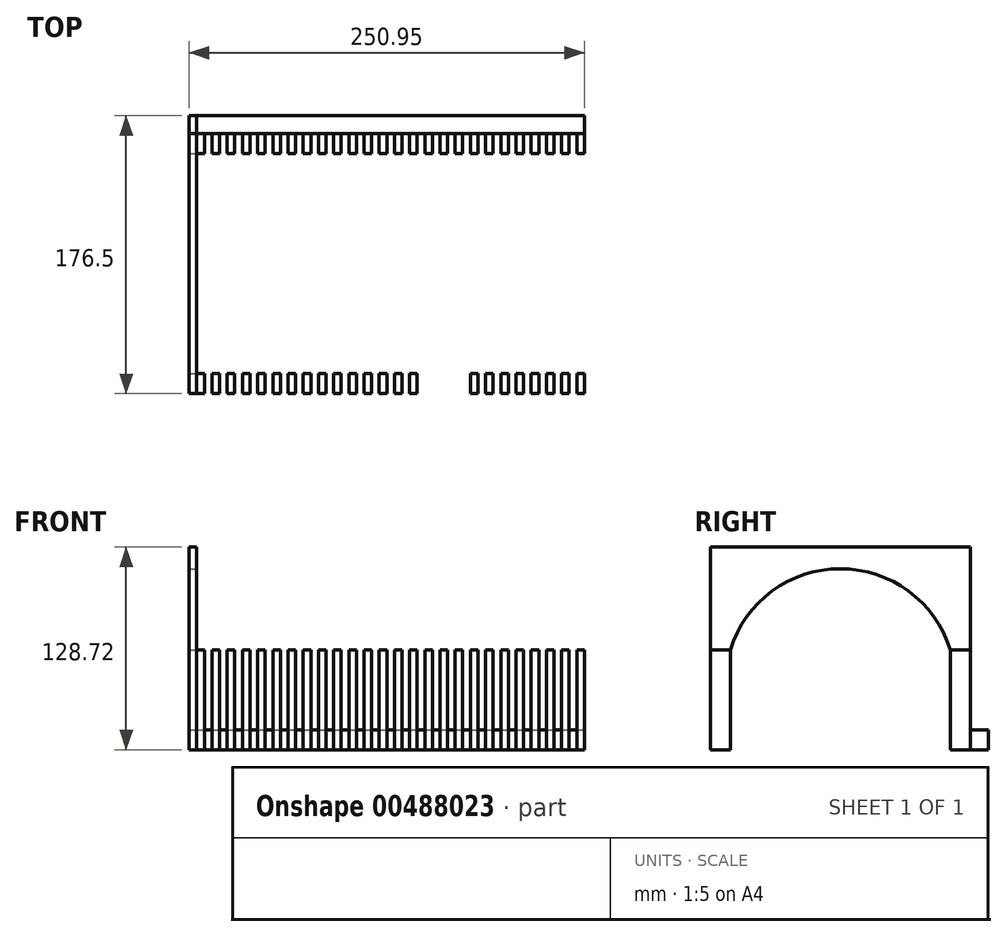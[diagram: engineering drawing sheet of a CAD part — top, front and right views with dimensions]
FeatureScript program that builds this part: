
annotation { "Feature Type Name" : "Feature", "Feature Type Description" : "" }
export const myFeature = defineFeature(function(context is Context, id is Id, definition is map)
    precondition{}
    {
        {
            var Q0;
            Q0=qCreatedBy(makeId("Top.planeOp"),FACE);
            var sketch = newSketch(context, id + "F0", { "sketchPlane" : qUnion([Q0])});
            skLineSegment(sketch, "E0.bottom", {"start": v(-94.37, 0) * mm, "end": v(-89.54, 0) * mm});
            skLineSegment(sketch, "E0.top", {"start": v(-94.37, 12.7) * mm, "end": v(-89.54, 12.7) * mm});
            skLineSegment(sketch, "E0.left", {"start": v(-94.37, 0) * mm, "end": v(-94.37, 12.7) * mm});
            skLineSegment(sketch, "E0.right", {"start": v(-89.54, 0) * mm, "end": v(-89.54, 12.7) * mm});
            skLineSegment(sketch, "E1.1.0.0", {"start": v(-84.71, 0) * mm, "end": v(-84.71, 12.7) * mm});
            skLineSegment(sketch, "E1.2.0.0", {"start": v(-79.89, 0) * mm, "end": v(-79.89, 12.7) * mm});
            skLineSegment(sketch, "E1.3.0.0", {"start": v(-75.06, 0) * mm, "end": v(-75.06, 12.7) * mm});
            skLineSegment(sketch, "E1.4.0.0", {"start": v(-70.24, 0) * mm, "end": v(-70.24, 12.7) * mm});
            skLineSegment(sketch, "E1.5.0.0", {"start": v(-65.4, 0) * mm, "end": v(-65.4, 12.7) * mm});
            skLineSegment(sketch, "E1.6.0.0", {"start": v(-60.58, 0) * mm, "end": v(-60.58, 12.7) * mm});
            skLineSegment(sketch, "E1.7.0.0", {"start": v(-55.76, 0) * mm, "end": v(-55.76, 12.7) * mm});
            skLineSegment(sketch, "E1.8.0.0", {"start": v(-50.93, 0) * mm, "end": v(-50.93, 12.7) * mm});
            skLineSegment(sketch, "E1.9.0.0", {"start": v(-46.1, 0) * mm, "end": v(-46.1, 12.7) * mm});
            skLineSegment(sketch, "E1.10.0.0", {"start": v(-41.28, 0) * mm, "end": v(-41.28, 12.7) * mm});
            skLineSegment(sketch, "E1.11.0.0", {"start": v(-36.45, 0) * mm, "end": v(-36.45, 12.7) * mm});
            skLineSegment(sketch, "E1.12.0.0", {"start": v(-31.63, 0) * mm, "end": v(-31.63, 12.7) * mm});
            skLineSegment(sketch, "E1.13.0.0", {"start": v(-26.8, 0) * mm, "end": v(-26.8, 12.7) * mm});
            skLineSegment(sketch, "E1.14.0.0", {"start": v(-21.98, 0) * mm, "end": v(-21.98, 12.7) * mm});
            skLineSegment(sketch, "E1.15.0.0", {"start": v(-17.15, 0) * mm, "end": v(-17.15, 12.7) * mm});
            skLineSegment(sketch, "E1.16.0.0", {"start": v(-12.32, 0) * mm, "end": v(-12.32, 12.7) * mm});
            skLineSegment(sketch, "E1.17.0.0", {"start": v(-7.5, 0) * mm, "end": v(-7.5, 12.7) * mm});
            skLineSegment(sketch, "E1.18.0.0", {"start": v(-2.67, 0) * mm, "end": v(-2.67, 12.7) * mm});
            skLineSegment(sketch, "E1.19.0.0", {"start": v(2.15, 0) * mm, "end": v(2.15, 12.7) * mm});
            skLineSegment(sketch, "E1.20.0.0", {"start": v(6.98, 0) * mm, "end": v(6.98, 12.7) * mm});
            skLineSegment(sketch, "E1.21.0.0", {"start": v(11.8, 0) * mm, "end": v(11.8, 12.7) * mm});
            skLineSegment(sketch, "E1.22.0.0", {"start": v(16.63, 0) * mm, "end": v(16.63, 12.7) * mm});
            skLineSegment(sketch, "E1.23.0.0", {"start": v(21.46, 0) * mm, "end": v(21.46, 12.7) * mm});
            skLineSegment(sketch, "E1.24.0.0", {"start": v(26.28, 0) * mm, "end": v(26.28, 12.7) * mm});
            skLineSegment(sketch, "E1.25.0.0", {"start": v(31.11, 0) * mm, "end": v(31.11, 12.7) * mm});
            skLineSegment(sketch, "E1.26.0.0", {"start": v(35.94, 0) * mm, "end": v(35.94, 12.7) * mm});
            skLineSegment(sketch, "E1.27.0.0", {"start": v(40.76, 0) * mm, "end": v(40.76, 12.7) * mm});
            skLineSegment(sketch, "E1.28.0.0", {"start": v(45.59, 0) * mm, "end": v(45.59, 12.7) * mm});
            skLineSegment(sketch, "E1.29.0.0", {"start": v(50.41, 0) * mm, "end": v(50.41, 12.7) * mm});
            skLineSegment(sketch, "E1.30.0.0", {"start": v(55.24, 0) * mm, "end": v(55.24, 12.7) * mm});
            skLineSegment(sketch, "E1.31.0.0", {"start": v(60.07, 0) * mm, "end": v(60.07, 12.7) * mm});
            skLineSegment(sketch, "E1.32.0.0", {"start": v(64.9, 0) * mm, "end": v(64.9, 12.7) * mm});
            skLineSegment(sketch, "E1.33.0.0", {"start": v(69.72, 0) * mm, "end": v(69.72, 12.7) * mm});
            skLineSegment(sketch, "E1.34.0.0", {"start": v(74.54, 0) * mm, "end": v(74.54, 12.7) * mm});
            skLineSegment(sketch, "E1.35.0.0", {"start": v(79.37, 0) * mm, "end": v(79.37, 12.7) * mm});
            skLineSegment(sketch, "E1.36.0.0", {"start": v(84.2, 0) * mm, "end": v(84.2, 12.7) * mm});
            skLineSegment(sketch, "E1.37.0.0", {"start": v(89.02, 0) * mm, "end": v(89.02, 12.7) * mm});
            skLineSegment(sketch, "E1.38.0.0", {"start": v(93.85, 0) * mm, "end": v(93.85, 12.7) * mm});
            skLineSegment(sketch, "E1.39.0.0", {"start": v(98.67, 0) * mm, "end": v(98.67, 12.7) * mm});
            skLineSegment(sketch, "E1.40.0.0", {"start": v(103.5, 0) * mm, "end": v(103.5, 12.7) * mm});
            skLineSegment(sketch, "E1.41.0.0", {"start": v(108.33, 0) * mm, "end": v(108.33, 12.7) * mm});
            skLineSegment(sketch, "E1.42.0.0", {"start": v(113.15, 0) * mm, "end": v(113.15, 12.7) * mm});
            skLineSegment(sketch, "E1.43.0.0", {"start": v(117.98, 0) * mm, "end": v(117.98, 12.7) * mm});
            skLineSegment(sketch, "E1.44.0.0", {"start": v(122.8, 0) * mm, "end": v(122.8, 12.7) * mm});
            skLineSegment(sketch, "E1.45.0.0", {"start": v(127.63, 0) * mm, "end": v(127.63, 12.7) * mm});
            skLineSegment(sketch, "E1.46.0.0", {"start": v(132.46, 0) * mm, "end": v(132.46, 12.7) * mm});
            skLineSegment(sketch, "E1.47.0.0", {"start": v(137.28, 0) * mm, "end": v(137.28, 12.7) * mm});
            skLineSegment(sketch, "E1.48.0.0", {"start": v(142.1, 0) * mm, "end": v(142.1, 12.7) * mm});
            skLineSegment(sketch, "E1.49.0.0", {"start": v(146.93, 0) * mm, "end": v(146.93, 12.7) * mm});
            skLineSegment(sketch, "E1.direction1", {"start": v(-89.54, 0) * mm, "end": v(-84.71, 0) * mm, "construction": true});
            skLineSegment(sketch, "E2", {"start": v(-84.71, 12.7) * mm, "end": v(-79.89, 12.7) * mm});
            skLineSegment(sketch, "E3", {"start": v(-75.06, 12.7) * mm, "end": v(-70.24, 12.7) * mm});
            skLineSegment(sketch, "E4", {"start": v(-65.4, 12.7) * mm, "end": v(-60.58, 12.7) * mm});
            skLineSegment(sketch, "E5", {"start": v(-55.76, 12.7) * mm, "end": v(-50.93, 12.7) * mm});
            skLineSegment(sketch, "E6", {"start": v(-46.1, 12.7) * mm, "end": v(-41.28, 12.7) * mm});
            skLineSegment(sketch, "E7", {"start": v(-36.45, 12.7) * mm, "end": v(-31.63, 12.7) * mm});
            skLineSegment(sketch, "E8", {"start": v(-26.8, 12.7) * mm, "end": v(-21.98, 12.7) * mm});
            skLineSegment(sketch, "E9", {"start": v(-17.15, 12.7) * mm, "end": v(-12.32, 12.7) * mm});
            skLineSegment(sketch, "E10", {"start": v(-7.5, 12.7) * mm, "end": v(-2.67, 12.7) * mm});
            skLineSegment(sketch, "E11", {"start": v(2.15, 12.7) * mm, "end": v(6.98, 12.7) * mm});
            skLineSegment(sketch, "E12", {"start": v(21.46, 12.7) * mm, "end": v(26.28, 12.7) * mm});
            skLineSegment(sketch, "E13", {"start": v(31.11, 12.7) * mm, "end": v(35.94, 12.7) * mm});
            skLineSegment(sketch, "E14", {"start": v(40.76, 12.7) * mm, "end": v(45.59, 12.7) * mm});
            skLineSegment(sketch, "E15", {"start": v(50.41, 12.7) * mm, "end": v(55.24, 12.7) * mm});
            skLineSegment(sketch, "E16", {"start": v(60.07, 12.7) * mm, "end": v(64.9, 12.7) * mm});
            skLineSegment(sketch, "E17", {"start": v(69.72, 12.7) * mm, "end": v(74.54, 12.7) * mm});
            skLineSegment(sketch, "E18", {"start": v(79.37, 12.7) * mm, "end": v(84.2, 12.7) * mm});
            skLineSegment(sketch, "E19", {"start": v(89.02, 12.7) * mm, "end": v(93.85, 12.7) * mm});
            skLineSegment(sketch, "E20", {"start": v(98.67, 12.7) * mm, "end": v(103.5, 12.7) * mm});
            skLineSegment(sketch, "E21", {"start": v(108.33, 12.7) * mm, "end": v(113.15, 12.7) * mm});
            skLineSegment(sketch, "E22", {"start": v(117.98, 12.7) * mm, "end": v(122.8, 12.7) * mm});
            skLineSegment(sketch, "E23", {"start": v(127.63, 12.7) * mm, "end": v(132.46, 12.7) * mm});
            skLineSegment(sketch, "E24", {"start": v(137.28, 12.7) * mm, "end": v(142.1, 12.7) * mm});
            skLineSegment(sketch, "E25", {"start": v(-84.71, 0) * mm, "end": v(-79.89, 0) * mm});
            skLineSegment(sketch, "E26", {"start": v(-75.06, 0) * mm, "end": v(-70.24, 0) * mm});
            skLineSegment(sketch, "E27", {"start": v(-65.4, 0) * mm, "end": v(-60.58, 0) * mm});
            skLineSegment(sketch, "E28", {"start": v(-55.76, 0) * mm, "end": v(-50.93, 0) * mm});
            skLineSegment(sketch, "E29", {"start": v(-46.1, 0) * mm, "end": v(-41.28, 0) * mm});
            skLineSegment(sketch, "E30", {"start": v(-36.45, 0) * mm, "end": v(-31.63, 0) * mm});
            skLineSegment(sketch, "E31", {"start": v(-26.8, 0) * mm, "end": v(-21.98, 0) * mm});
            skLineSegment(sketch, "E32", {"start": v(-17.15, 0) * mm, "end": v(-12.32, 0) * mm});
            skLineSegment(sketch, "E33", {"start": v(-7.5, 0) * mm, "end": v(-2.67, 0) * mm});
            skLineSegment(sketch, "E34", {"start": v(2.15, 0) * mm, "end": v(6.98, 0) * mm});
            skLineSegment(sketch, "E35", {"start": v(21.46, 0) * mm, "end": v(26.28, 0) * mm});
            skLineSegment(sketch, "E36", {"start": v(11.8, 12.7) * mm, "end": v(16.63, 12.7) * mm});
            skLineSegment(sketch, "E37", {"start": v(16.63, 0) * mm, "end": v(11.8, 0) * mm});
            skLineSegment(sketch, "E38", {"start": v(31.11, 0) * mm, "end": v(35.94, 0) * mm});
            skLineSegment(sketch, "E39", {"start": v(40.76, 0) * mm, "end": v(45.59, 0) * mm});
            skLineSegment(sketch, "E40", {"start": v(50.41, 0) * mm, "end": v(55.24, 0) * mm});
            skLineSegment(sketch, "E41", {"start": v(60.07, 0) * mm, "end": v(64.9, 0) * mm});
            skLineSegment(sketch, "E42", {"start": v(69.72, 0) * mm, "end": v(74.54, 0) * mm});
            skLineSegment(sketch, "E43", {"start": v(79.37, 0) * mm, "end": v(84.2, 0) * mm});
            skLineSegment(sketch, "E44", {"start": v(89.02, 0) * mm, "end": v(93.85, 0) * mm});
            skLineSegment(sketch, "E45", {"start": v(98.67, 0) * mm, "end": v(103.5, 0) * mm});
            skLineSegment(sketch, "E46", {"start": v(108.33, 0) * mm, "end": v(113.15, 0) * mm});
            skLineSegment(sketch, "E47", {"start": v(117.98, 0) * mm, "end": v(122.8, 0) * mm});
            skLineSegment(sketch, "E48", {"start": v(127.63, 0) * mm, "end": v(132.46, 0) * mm});
            skLineSegment(sketch, "E49", {"start": v(137.28, 0) * mm, "end": v(142.1, 0) * mm});
            skLineSegment(sketch, "E50", {"start": v(146.93, 12.7) * mm, "end": v(151.76, 12.7) * mm});
            skLineSegment(sketch, "E51", {"start": v(151.76, 12.7) * mm, "end": v(151.76, 0) * mm});
            skLineSegment(sketch, "E52", {"start": v(151.76, 0) * mm, "end": v(146.93, 0) * mm});
            skLineSegment(sketch, "E53", {"start": v(-94.37, 0) * mm, "end": v(151.76, 0) * mm, "construction": true});
            skLineSegment(sketch, "E54.bottom", {"start": v(-94.37, 12.7) * mm, "end": v(151.76, 12.7) * mm});
            skLineSegment(sketch, "E54.top", {"start": v(-94.37, 24.1) * mm, "end": v(151.76, 24.1) * mm});
            skLineSegment(sketch, "E54.left", {"start": v(-94.37, 12.7) * mm, "end": v(-94.37, 24.1) * mm});
            skLineSegment(sketch, "E54.right", {"start": v(151.76, 12.7) * mm, "end": v(151.76, 24.1) * mm});
            skLineSegment(sketch, "E55", {"start": v(-124.36, -69.85) * mm, "end": v(197.2, -69.85) * mm, "construction": true});
            skLineSegment(sketch, "E56.MirrorCS", {"start": v(-89.54, -139.7) * mm, "end": v(-84.71, -139.7) * mm, "construction": true});
            skLineSegment(sketch, "E57.MirrorCS", {"start": v(108.33, -139.7) * mm, "end": v(113.15, -139.7) * mm});
            skLineSegment(sketch, "E58.MirrorCS", {"start": v(-55.76, -139.7) * mm, "end": v(-50.93, -139.7) * mm});
            skLineSegment(sketch, "E59.MirrorCS", {"start": v(-94.37, -139.7) * mm, "end": v(-89.54, -139.7) * mm});
            skLineSegment(sketch, "E60.MirrorCS", {"start": v(79.37, -139.7) * mm, "end": v(84.2, -139.7) * mm});
            skLineSegment(sketch, "E61.MirrorCS", {"start": v(108.33, -152.4) * mm, "end": v(113.15, -152.4) * mm});
            skLineSegment(sketch, "E62.MirrorCS", {"start": v(-26.8, -152.4) * mm, "end": v(-21.98, -152.4) * mm});
            skLineSegment(sketch, "E63.MirrorCS", {"start": v(2.15, -139.7) * mm, "end": v(6.98, -139.7) * mm});
            skLineSegment(sketch, "E64.MirrorCS", {"start": v(-7.5, -139.7) * mm, "end": v(-2.67, -139.7) * mm});
            skLineSegment(sketch, "E65.MirrorCS", {"start": v(-55.76, -152.4) * mm, "end": v(-50.93, -152.4) * mm});
            skLineSegment(sketch, "E66.MirrorCS", {"start": v(98.67, -139.7) * mm, "end": v(103.5, -139.7) * mm});
            skLineSegment(sketch, "E67.MirrorCS", {"start": v(40.76, -152.4) * mm, "end": v(45.59, -152.4) * mm});
            skLineSegment(sketch, "E68.MirrorCS", {"start": v(-94.37, -139.7) * mm, "end": v(151.76, -139.7) * mm, "construction": true});
            skLineSegment(sketch, "E69.MirrorCS", {"start": v(31.11, -152.4) * mm, "end": v(35.94, -152.4) * mm});
            skLineSegment(sketch, "E70.MirrorCS", {"start": v(-46.1, -139.7) * mm, "end": v(-41.28, -139.7) * mm});
            skLineSegment(sketch, "E71.MirrorCS", {"start": v(11.8, -152.4) * mm, "end": v(16.63, -152.4) * mm});
            skLineSegment(sketch, "E72.MirrorCS", {"start": v(21.46, -139.7) * mm, "end": v(26.28, -139.7) * mm});
            skLineSegment(sketch, "E73.MirrorCS", {"start": v(-75.06, -152.4) * mm, "end": v(-70.24, -152.4) * mm});
            skLineSegment(sketch, "E74.MirrorCS", {"start": v(146.93, -152.4) * mm, "end": v(151.76, -152.4) * mm});
            skLineSegment(sketch, "E75.MirrorCS", {"start": v(-84.71, -152.4) * mm, "end": v(-79.89, -152.4) * mm});
            skLineSegment(sketch, "E76.MirrorCS", {"start": v(2.15, -152.4) * mm, "end": v(6.98, -152.4) * mm});
            skLineSegment(sketch, "E77.MirrorCS", {"start": v(-17.15, -152.4) * mm, "end": v(-12.32, -152.4) * mm});
            skLineSegment(sketch, "E78.MirrorCS", {"start": v(40.76, -139.7) * mm, "end": v(45.59, -139.7) * mm});
            skLineSegment(sketch, "E79.MirrorCS", {"start": v(-36.45, -152.4) * mm, "end": v(-31.63, -152.4) * mm});
            skLineSegment(sketch, "E80.MirrorCS", {"start": v(127.63, -152.4) * mm, "end": v(132.46, -152.4) * mm});
            skLineSegment(sketch, "E81.MirrorCS", {"start": v(127.63, -139.7) * mm, "end": v(132.46, -139.7) * mm});
            skLineSegment(sketch, "E82.MirrorCS", {"start": v(16.63, -139.7) * mm, "end": v(11.8, -139.7) * mm});
            skLineSegment(sketch, "E83.MirrorCS", {"start": v(-94.37, -152.4) * mm, "end": v(-89.54, -152.4) * mm});
            skLineSegment(sketch, "E84.MirrorCS", {"start": v(117.98, -139.7) * mm, "end": v(122.8, -139.7) * mm});
            skLineSegment(sketch, "E85.MirrorCS", {"start": v(137.28, -152.4) * mm, "end": v(142.1, -152.4) * mm});
            skLineSegment(sketch, "E86.MirrorCS", {"start": v(79.37, -152.4) * mm, "end": v(84.2, -152.4) * mm});
            skLineSegment(sketch, "E87.MirrorCS", {"start": v(31.11, -139.7) * mm, "end": v(35.94, -139.7) * mm});
            skLineSegment(sketch, "E88.MirrorCS", {"start": v(-65.4, -152.4) * mm, "end": v(-60.58, -152.4) * mm});
            skLineSegment(sketch, "E89.MirrorCS", {"start": v(-46.1, -152.4) * mm, "end": v(-41.28, -152.4) * mm});
            skLineSegment(sketch, "E90.MirrorCS", {"start": v(-26.8, -139.7) * mm, "end": v(-21.98, -139.7) * mm});
            skLineSegment(sketch, "E91.MirrorCS", {"start": v(-94.37, -152.4) * mm, "end": v(151.76, -152.4) * mm});
            skLineSegment(sketch, "E92.MirrorCS", {"start": v(117.98, -152.4) * mm, "end": v(122.8, -152.4) * mm});
            skLineSegment(sketch, "E93.MirrorCS", {"start": v(89.02, -139.7) * mm, "end": v(93.85, -139.7) * mm});
            skLineSegment(sketch, "E94.MirrorCS", {"start": v(21.46, -152.4) * mm, "end": v(26.28, -152.4) * mm});
            skLineSegment(sketch, "E95.MirrorCS", {"start": v(69.72, -152.4) * mm, "end": v(74.54, -152.4) * mm});
            skLineSegment(sketch, "E96.MirrorCS", {"start": v(-65.4, -139.7) * mm, "end": v(-60.58, -139.7) * mm});
            skLineSegment(sketch, "E97.MirrorCS", {"start": v(-17.15, -139.7) * mm, "end": v(-12.32, -139.7) * mm});
            skLineSegment(sketch, "E98.MirrorCS", {"start": v(-84.71, -139.7) * mm, "end": v(-79.89, -139.7) * mm});
            skLineSegment(sketch, "E99.MirrorCS", {"start": v(60.07, -152.4) * mm, "end": v(64.9, -152.4) * mm});
            skLineSegment(sketch, "E100.MirrorCS", {"start": v(60.07, -139.7) * mm, "end": v(64.9, -139.7) * mm});
            skLineSegment(sketch, "E101.MirrorCS", {"start": v(137.28, -139.7) * mm, "end": v(142.1, -139.7) * mm});
            skLineSegment(sketch, "E102.MirrorCS", {"start": v(50.41, -152.4) * mm, "end": v(55.24, -152.4) * mm});
            skLineSegment(sketch, "E103.MirrorCS", {"start": v(89.02, -152.4) * mm, "end": v(93.85, -152.4) * mm});
            skLineSegment(sketch, "E104.MirrorCS", {"start": v(50.41, -139.7) * mm, "end": v(55.24, -139.7) * mm});
            skLineSegment(sketch, "E105.MirrorCS", {"start": v(-75.06, -139.7) * mm, "end": v(-70.24, -139.7) * mm});
            skLineSegment(sketch, "E106.MirrorCS", {"start": v(-7.5, -152.4) * mm, "end": v(-2.67, -152.4) * mm});
            skLineSegment(sketch, "E107.MirrorCS", {"start": v(69.72, -139.7) * mm, "end": v(74.54, -139.7) * mm});
            skLineSegment(sketch, "E108.MirrorCS", {"start": v(-36.45, -139.7) * mm, "end": v(-31.63, -139.7) * mm});
            skLineSegment(sketch, "E109.MirrorCS", {"start": v(98.67, -152.4) * mm, "end": v(103.5, -152.4) * mm});
            skLineSegment(sketch, "E110.MirrorCS", {"start": v(151.76, -139.7) * mm, "end": v(146.93, -139.7) * mm});
            skLineSegment(sketch, "E111.MirrorCS", {"start": v(151.76, -152.4) * mm, "end": v(151.76, -163.8) * mm});
            skLineSegment(sketch, "E112.MirrorCS", {"start": v(60.07, -139.7) * mm, "end": v(60.07, -152.4) * mm});
            skLineSegment(sketch, "E113.MirrorCS", {"start": v(137.28, -139.7) * mm, "end": v(137.28, -152.4) * mm});
            skLineSegment(sketch, "E114.MirrorCS", {"start": v(93.85, -139.7) * mm, "end": v(93.85, -152.4) * mm});
            skLineSegment(sketch, "E115.MirrorCS", {"start": v(55.24, -139.7) * mm, "end": v(55.24, -152.4) * mm});
            skLineSegment(sketch, "E116.MirrorCS", {"start": v(132.46, -139.7) * mm, "end": v(132.46, -152.4) * mm});
            skLineSegment(sketch, "E117.MirrorCS", {"start": v(11.8, -139.7) * mm, "end": v(11.8, -152.4) * mm});
            skLineSegment(sketch, "E118.MirrorCS", {"start": v(50.41, -139.7) * mm, "end": v(50.41, -152.4) * mm});
            skLineSegment(sketch, "E119.MirrorCS", {"start": v(6.98, -139.7) * mm, "end": v(6.98, -152.4) * mm});
            skLineSegment(sketch, "E120.MirrorCS", {"start": v(84.2, -139.7) * mm, "end": v(84.2, -152.4) * mm});
            skLineSegment(sketch, "E121.MirrorCS", {"start": v(-65.4, -139.7) * mm, "end": v(-65.4, -152.4) * mm});
            skLineSegment(sketch, "E122.MirrorCS", {"start": v(-94.37, -139.7) * mm, "end": v(-94.37, -152.4) * mm});
            skLineSegment(sketch, "E123.MirrorCS", {"start": v(-31.63, -139.7) * mm, "end": v(-31.63, -152.4) * mm});
            skLineSegment(sketch, "E124.MirrorCS", {"start": v(-36.45, -139.7) * mm, "end": v(-36.45, -152.4) * mm});
            skLineSegment(sketch, "E125.MirrorCS", {"start": v(45.59, -139.7) * mm, "end": v(45.59, -152.4) * mm});
            skLineSegment(sketch, "E126.MirrorCS", {"start": v(2.15, -139.7) * mm, "end": v(2.15, -152.4) * mm});
            skLineSegment(sketch, "E127.MirrorCS", {"start": v(146.93, -139.7) * mm, "end": v(146.93, -152.4) * mm});
            skLineSegment(sketch, "E128.MirrorCS", {"start": v(-94.37, -163.8) * mm, "end": v(151.76, -163.8) * mm});
            skLineSegment(sketch, "E129.MirrorCS", {"start": v(26.28, -139.7) * mm, "end": v(26.28, -152.4) * mm});
            skLineSegment(sketch, "E130.MirrorCS", {"start": v(103.5, -139.7) * mm, "end": v(103.5, -152.4) * mm});
            skLineSegment(sketch, "E131.MirrorCS", {"start": v(-7.5, -139.7) * mm, "end": v(-7.5, -152.4) * mm});
            skLineSegment(sketch, "E132.MirrorCS", {"start": v(-94.37, -152.4) * mm, "end": v(-94.37, -163.8) * mm});
            skLineSegment(sketch, "E133.MirrorCS", {"start": v(-60.58, -139.7) * mm, "end": v(-60.58, -152.4) * mm});
            skLineSegment(sketch, "E134.MirrorCS", {"start": v(142.1, -139.7) * mm, "end": v(142.1, -152.4) * mm});
            skLineSegment(sketch, "E135.MirrorCS", {"start": v(64.9, -139.7) * mm, "end": v(64.9, -152.4) * mm});
            skLineSegment(sketch, "E136.MirrorCS", {"start": v(-70.24, -139.7) * mm, "end": v(-70.24, -152.4) * mm});
            skLineSegment(sketch, "E137.MirrorCS", {"start": v(-84.71, -139.7) * mm, "end": v(-84.71, -152.4) * mm});
            skLineSegment(sketch, "E138.MirrorCS", {"start": v(-12.32, -139.7) * mm, "end": v(-12.32, -152.4) * mm});
            skLineSegment(sketch, "E139.MirrorCS", {"start": v(-55.76, -139.7) * mm, "end": v(-55.76, -152.4) * mm});
            skLineSegment(sketch, "E140.MirrorCS", {"start": v(122.8, -139.7) * mm, "end": v(122.8, -152.4) * mm});
            skLineSegment(sketch, "E141.MirrorCS", {"start": v(16.63, -139.7) * mm, "end": v(16.63, -152.4) * mm});
            skLineSegment(sketch, "E142.MirrorCS", {"start": v(79.37, -139.7) * mm, "end": v(79.37, -152.4) * mm});
            skLineSegment(sketch, "E143.MirrorCS", {"start": v(-21.98, -139.7) * mm, "end": v(-21.98, -152.4) * mm});
            skLineSegment(sketch, "E144.MirrorCS", {"start": v(-50.93, -139.7) * mm, "end": v(-50.93, -152.4) * mm});
            skLineSegment(sketch, "E145.MirrorCS", {"start": v(-41.28, -139.7) * mm, "end": v(-41.28, -152.4) * mm});
            skLineSegment(sketch, "E146.MirrorCS", {"start": v(21.46, -139.7) * mm, "end": v(21.46, -152.4) * mm});
            skLineSegment(sketch, "E147.MirrorCS", {"start": v(98.67, -139.7) * mm, "end": v(98.67, -152.4) * mm});
            skLineSegment(sketch, "E148.MirrorCS", {"start": v(-26.8, -139.7) * mm, "end": v(-26.8, -152.4) * mm});
            skLineSegment(sketch, "E149.MirrorCS", {"start": v(117.98, -139.7) * mm, "end": v(117.98, -152.4) * mm});
            skLineSegment(sketch, "E150.MirrorCS", {"start": v(74.54, -139.7) * mm, "end": v(74.54, -152.4) * mm});
            skLineSegment(sketch, "E151.MirrorCS", {"start": v(127.63, -139.7) * mm, "end": v(127.63, -152.4) * mm});
            skLineSegment(sketch, "E152.MirrorCS", {"start": v(-79.89, -139.7) * mm, "end": v(-79.89, -152.4) * mm});
            skLineSegment(sketch, "E153.MirrorCS", {"start": v(113.15, -139.7) * mm, "end": v(113.15, -152.4) * mm});
            skLineSegment(sketch, "E154.MirrorCS", {"start": v(35.94, -139.7) * mm, "end": v(35.94, -152.4) * mm});
            skLineSegment(sketch, "E155.MirrorCS", {"start": v(69.72, -139.7) * mm, "end": v(69.72, -152.4) * mm});
            skLineSegment(sketch, "E156.MirrorCS", {"start": v(151.76, -152.4) * mm, "end": v(151.76, -139.7) * mm});
            skLineSegment(sketch, "E157.MirrorCS", {"start": v(-75.06, -139.7) * mm, "end": v(-75.06, -152.4) * mm});
            skLineSegment(sketch, "E158.MirrorCS", {"start": v(108.33, -139.7) * mm, "end": v(108.33, -152.4) * mm});
            skLineSegment(sketch, "E159.MirrorCS", {"start": v(89.02, -139.7) * mm, "end": v(89.02, -152.4) * mm});
            skLineSegment(sketch, "E160.MirrorCS", {"start": v(31.11, -139.7) * mm, "end": v(31.11, -152.4) * mm});
            skLineSegment(sketch, "E161.MirrorCS", {"start": v(-2.67, -139.7) * mm, "end": v(-2.67, -152.4) * mm});
            skLineSegment(sketch, "E162.MirrorCS", {"start": v(40.76, -139.7) * mm, "end": v(40.76, -152.4) * mm});
            skLineSegment(sketch, "E163.MirrorCS", {"start": v(-17.15, -139.7) * mm, "end": v(-17.15, -152.4) * mm});
            skLineSegment(sketch, "E164.MirrorCS", {"start": v(-89.54, -139.7) * mm, "end": v(-89.54, -152.4) * mm});
            skLineSegment(sketch, "E165.MirrorCS", {"start": v(-46.1, -139.7) * mm, "end": v(-46.1, -152.4) * mm});
            skSolve(sketch);
        }
        {
            var Q0;
            Q0=makeQuery(id+"F0.imprint","IMPRINT",FACE,{"disambiguationData":[TD([[makeQuery(id+"F0.imprint","IMPRINT",EDGE,{"derivedFrom":sQuery(id+"F0.wireOp",EDGE,"E54.top")}),-1.0]])]});
            var Q1;
            {var subQ2=sQuery(id+"F0.wireOp",EDGE,"E92.MirrorCS");Q1=makeQuery(id+"F0.imprint","IMPRINT",FACE,{"disambiguationData":[TD([[makeQuery(id+"F0.imprint","IMPRINT",EDGE,{"derivedFrom":subQ2}),-1.0]])]});}
            extrude(context, id + "F1", {"entities" : qUnion([Q0, Q1]), "depth" : 12.7 * mm});
        }
        {
            var Q0;
            Q0=makeQuery(id+"F0.imprint","IMPRINT",FACE,{"disambiguationData":[TD([[makeQuery(id+"F0.imprint","IMPRINT",EDGE,{"derivedFrom":sQuery(id+"F0.wireOp",EDGE,"E0.bottom")}),1.0]])]});
            var Q1;
            {var subQ0=sQuery(id+"F0.wireOp",EDGE,"E1.1.0.0");Q1=makeQuery(id+"F0.imprint","IMPRINT",FACE,{"disambiguationData":[TD([[makeQuery(id+"F0.imprint","IMPRINT",EDGE,{"derivedFrom":subQ0}),-1.0]])]});}
            var Q2;
            {var subQ0=sQuery(id+"F0.wireOp",EDGE,"E1.3.0.0");Q2=makeQuery(id+"F0.imprint","IMPRINT",FACE,{"disambiguationData":[TD([[makeQuery(id+"F0.imprint","IMPRINT",EDGE,{"derivedFrom":subQ0}),-1.0]])]});}
            var Q3;
            {var subQ0=sQuery(id+"F0.wireOp",EDGE,"E1.5.0.0");Q3=makeQuery(id+"F0.imprint","IMPRINT",FACE,{"disambiguationData":[TD([[makeQuery(id+"F0.imprint","IMPRINT",EDGE,{"derivedFrom":subQ0}),-1.0]])]});}
            var Q4;
            {var subQ0=sQuery(id+"F0.wireOp",EDGE,"E1.7.0.0");Q4=makeQuery(id+"F0.imprint","IMPRINT",FACE,{"disambiguationData":[TD([[makeQuery(id+"F0.imprint","IMPRINT",EDGE,{"derivedFrom":subQ0}),-1.0]])]});}
            var Q5;
            {var subQ0=sQuery(id+"F0.wireOp",EDGE,"E1.9.0.0");Q5=makeQuery(id+"F0.imprint","IMPRINT",FACE,{"disambiguationData":[TD([[makeQuery(id+"F0.imprint","IMPRINT",EDGE,{"derivedFrom":subQ0}),-1.0]])]});}
            var Q6;
            {var subQ0=sQuery(id+"F0.wireOp",EDGE,"E1.11.0.0");Q6=makeQuery(id+"F0.imprint","IMPRINT",FACE,{"disambiguationData":[TD([[makeQuery(id+"F0.imprint","IMPRINT",EDGE,{"derivedFrom":subQ0}),-1.0]])]});}
            var Q7;
            {var subQ0=sQuery(id+"F0.wireOp",EDGE,"E1.13.0.0");Q7=makeQuery(id+"F0.imprint","IMPRINT",FACE,{"disambiguationData":[TD([[makeQuery(id+"F0.imprint","IMPRINT",EDGE,{"derivedFrom":subQ0}),-1.0]])]});}
            var Q8;
            {var subQ0=sQuery(id+"F0.wireOp",EDGE,"E1.15.0.0");Q8=makeQuery(id+"F0.imprint","IMPRINT",FACE,{"disambiguationData":[TD([[makeQuery(id+"F0.imprint","IMPRINT",EDGE,{"derivedFrom":subQ0}),-1.0]])]});}
            var Q9;
            {var subQ0=sQuery(id+"F0.wireOp",EDGE,"E1.17.0.0");Q9=makeQuery(id+"F0.imprint","IMPRINT",FACE,{"disambiguationData":[TD([[makeQuery(id+"F0.imprint","IMPRINT",EDGE,{"derivedFrom":subQ0}),-1.0]])]});}
            var Q10;
            {var subQ0=sQuery(id+"F0.wireOp",EDGE,"E1.19.0.0");Q10=makeQuery(id+"F0.imprint","IMPRINT",FACE,{"disambiguationData":[TD([[makeQuery(id+"F0.imprint","IMPRINT",EDGE,{"derivedFrom":subQ0}),-1.0]])]});}
            var Q11;
            {var subQ0=sQuery(id+"F0.wireOp",EDGE,"E1.21.0.0");Q11=makeQuery(id+"F0.imprint","IMPRINT",FACE,{"disambiguationData":[TD([[makeQuery(id+"F0.imprint","IMPRINT",EDGE,{"derivedFrom":subQ0}),-1.0]])]});}
            var Q12;
            {var subQ0=sQuery(id+"F0.wireOp",EDGE,"E1.23.0.0");Q12=makeQuery(id+"F0.imprint","IMPRINT",FACE,{"disambiguationData":[TD([[makeQuery(id+"F0.imprint","IMPRINT",EDGE,{"derivedFrom":subQ0}),-1.0]])]});}
            var Q13;
            {var subQ0=sQuery(id+"F0.wireOp",EDGE,"E1.25.0.0");Q13=makeQuery(id+"F0.imprint","IMPRINT",FACE,{"disambiguationData":[TD([[makeQuery(id+"F0.imprint","IMPRINT",EDGE,{"derivedFrom":subQ0}),-1.0]])]});}
            var Q14;
            {var subQ0=sQuery(id+"F0.wireOp",EDGE,"E1.27.0.0");Q14=makeQuery(id+"F0.imprint","IMPRINT",FACE,{"disambiguationData":[TD([[makeQuery(id+"F0.imprint","IMPRINT",EDGE,{"derivedFrom":subQ0}),-1.0]])]});}
            var Q15;
            {var subQ0=sQuery(id+"F0.wireOp",EDGE,"E1.29.0.0");Q15=makeQuery(id+"F0.imprint","IMPRINT",FACE,{"disambiguationData":[TD([[makeQuery(id+"F0.imprint","IMPRINT",EDGE,{"derivedFrom":subQ0}),-1.0]])]});}
            var Q16;
            {var subQ0=sQuery(id+"F0.wireOp",EDGE,"E1.31.0.0");Q16=makeQuery(id+"F0.imprint","IMPRINT",FACE,{"disambiguationData":[TD([[makeQuery(id+"F0.imprint","IMPRINT",EDGE,{"derivedFrom":subQ0}),-1.0]])]});}
            var Q17;
            {var subQ0=sQuery(id+"F0.wireOp",EDGE,"E1.33.0.0");Q17=makeQuery(id+"F0.imprint","IMPRINT",FACE,{"disambiguationData":[TD([[makeQuery(id+"F0.imprint","IMPRINT",EDGE,{"derivedFrom":subQ0}),-1.0]])]});}
            var Q18;
            {var subQ0=sQuery(id+"F0.wireOp",EDGE,"E1.35.0.0");Q18=makeQuery(id+"F0.imprint","IMPRINT",FACE,{"disambiguationData":[TD([[makeQuery(id+"F0.imprint","IMPRINT",EDGE,{"derivedFrom":subQ0}),-1.0]])]});}
            var Q19;
            {var subQ0=sQuery(id+"F0.wireOp",EDGE,"E1.37.0.0");Q19=makeQuery(id+"F0.imprint","IMPRINT",FACE,{"disambiguationData":[TD([[makeQuery(id+"F0.imprint","IMPRINT",EDGE,{"derivedFrom":subQ0}),-1.0]])]});}
            var Q20;
            {var subQ0=sQuery(id+"F0.wireOp",EDGE,"E1.39.0.0");Q20=makeQuery(id+"F0.imprint","IMPRINT",FACE,{"disambiguationData":[TD([[makeQuery(id+"F0.imprint","IMPRINT",EDGE,{"derivedFrom":subQ0}),-1.0]])]});}
            var Q21;
            {var subQ0=sQuery(id+"F0.wireOp",EDGE,"E1.41.0.0");Q21=makeQuery(id+"F0.imprint","IMPRINT",FACE,{"disambiguationData":[TD([[makeQuery(id+"F0.imprint","IMPRINT",EDGE,{"derivedFrom":subQ0}),-1.0]])]});}
            var Q22;
            {var subQ0=sQuery(id+"F0.wireOp",EDGE,"E1.43.0.0");Q22=makeQuery(id+"F0.imprint","IMPRINT",FACE,{"disambiguationData":[TD([[makeQuery(id+"F0.imprint","IMPRINT",EDGE,{"derivedFrom":subQ0}),-1.0]])]});}
            var Q23;
            {var subQ0=sQuery(id+"F0.wireOp",EDGE,"E1.45.0.0");Q23=makeQuery(id+"F0.imprint","IMPRINT",FACE,{"disambiguationData":[TD([[makeQuery(id+"F0.imprint","IMPRINT",EDGE,{"derivedFrom":subQ0}),-1.0]])]});}
            var Q24;
            {var subQ0=sQuery(id+"F0.wireOp",EDGE,"E1.47.0.0");Q24=makeQuery(id+"F0.imprint","IMPRINT",FACE,{"disambiguationData":[TD([[makeQuery(id+"F0.imprint","IMPRINT",EDGE,{"derivedFrom":subQ0}),-1.0]])]});}
            var Q25;
            {var subQ0=sQuery(id+"F0.wireOp",EDGE,"E1.49.0.0");Q25=makeQuery(id+"F0.imprint","IMPRINT",FACE,{"disambiguationData":[TD([[makeQuery(id+"F0.imprint","IMPRINT",EDGE,{"derivedFrom":subQ0}),-1.0]])]});}
            var Q26;
            Q26=makeQuery(id+"F0.imprint","IMPRINT",FACE,{"disambiguationData":[TD([[makeQuery(id+"F0.imprint","IMPRINT",EDGE,{"derivedFrom":sQuery(id+"F0.wireOp",EDGE,"E57.MirrorCS")}),-1.0]])]});
            var Q27;
            Q27=makeQuery(id+"F0.imprint","IMPRINT",FACE,{"disambiguationData":[TD([[makeQuery(id+"F0.imprint","IMPRINT",EDGE,{"derivedFrom":sQuery(id+"F0.wireOp",EDGE,"E58.MirrorCS")}),-1.0]])]});
            var Q28;
            Q28=makeQuery(id+"F0.imprint","IMPRINT",FACE,{"disambiguationData":[TD([[makeQuery(id+"F0.imprint","IMPRINT",EDGE,{"derivedFrom":sQuery(id+"F0.wireOp",EDGE,"E59.MirrorCS")}),-1.0]])]});
            var Q29;
            Q29=makeQuery(id+"F0.imprint","IMPRINT",FACE,{"disambiguationData":[TD([[makeQuery(id+"F0.imprint","IMPRINT",EDGE,{"derivedFrom":sQuery(id+"F0.wireOp",EDGE,"E60.MirrorCS")}),-1.0]])]});
            var Q30;
            Q30=makeQuery(id+"F0.imprint","IMPRINT",FACE,{"disambiguationData":[TD([[makeQuery(id+"F0.imprint","IMPRINT",EDGE,{"derivedFrom":sQuery(id+"F0.wireOp",EDGE,"E63.MirrorCS")}),-1.0]])]});
            var Q31;
            Q31=makeQuery(id+"F0.imprint","IMPRINT",FACE,{"disambiguationData":[TD([[makeQuery(id+"F0.imprint","IMPRINT",EDGE,{"derivedFrom":sQuery(id+"F0.wireOp",EDGE,"E64.MirrorCS")}),-1.0]])]});
            var Q32;
            Q32=makeQuery(id+"F0.imprint","IMPRINT",FACE,{"disambiguationData":[TD([[makeQuery(id+"F0.imprint","IMPRINT",EDGE,{"derivedFrom":sQuery(id+"F0.wireOp",EDGE,"E66.MirrorCS")}),-1.0]])]});
            var Q33;
            Q33=makeQuery(id+"F0.imprint","IMPRINT",FACE,{"disambiguationData":[TD([[makeQuery(id+"F0.imprint","IMPRINT",EDGE,{"derivedFrom":sQuery(id+"F0.wireOp",EDGE,"E70.MirrorCS")}),-1.0]])]});
            var Q34;
            Q34=makeQuery(id+"F0.imprint","IMPRINT",FACE,{"disambiguationData":[TD([[makeQuery(id+"F0.imprint","IMPRINT",EDGE,{"derivedFrom":sQuery(id+"F0.wireOp",EDGE,"E72.MirrorCS")}),-1.0]])]});
            var Q35;
            Q35=makeQuery(id+"F0.imprint","IMPRINT",FACE,{"disambiguationData":[TD([[makeQuery(id+"F0.imprint","IMPRINT",EDGE,{"derivedFrom":sQuery(id+"F0.wireOp",EDGE,"E78.MirrorCS")}),-1.0]])]});
            var Q36;
            Q36=makeQuery(id+"F0.imprint","IMPRINT",FACE,{"disambiguationData":[TD([[makeQuery(id+"F0.imprint","IMPRINT",EDGE,{"derivedFrom":sQuery(id+"F0.wireOp",EDGE,"E81.MirrorCS")}),-1.0]])]});
            var Q37;
            Q37=makeQuery(id+"F0.imprint","IMPRINT",FACE,{"disambiguationData":[TD([[makeQuery(id+"F0.imprint","IMPRINT",EDGE,{"derivedFrom":sQuery(id+"F0.wireOp",EDGE,"E82.MirrorCS")}),1.0]])]});
            var Q38;
            Q38=makeQuery(id+"F0.imprint","IMPRINT",FACE,{"disambiguationData":[TD([[makeQuery(id+"F0.imprint","IMPRINT",EDGE,{"derivedFrom":sQuery(id+"F0.wireOp",EDGE,"E84.MirrorCS")}),-1.0]])]});
            var Q39;
            Q39=makeQuery(id+"F0.imprint","IMPRINT",FACE,{"disambiguationData":[TD([[makeQuery(id+"F0.imprint","IMPRINT",EDGE,{"derivedFrom":sQuery(id+"F0.wireOp",EDGE,"E87.MirrorCS")}),-1.0]])]});
            var Q40;
            Q40=makeQuery(id+"F0.imprint","IMPRINT",FACE,{"disambiguationData":[TD([[makeQuery(id+"F0.imprint","IMPRINT",EDGE,{"derivedFrom":sQuery(id+"F0.wireOp",EDGE,"E90.MirrorCS")}),-1.0]])]});
            var Q41;
            Q41=makeQuery(id+"F0.imprint","IMPRINT",FACE,{"disambiguationData":[TD([[makeQuery(id+"F0.imprint","IMPRINT",EDGE,{"derivedFrom":sQuery(id+"F0.wireOp",EDGE,"E98.MirrorCS")}),-1.0]])]});
            var Q42;
            Q42=makeQuery(id+"F0.imprint","IMPRINT",FACE,{"disambiguationData":[TD([[makeQuery(id+"F0.imprint","IMPRINT",EDGE,{"derivedFrom":sQuery(id+"F0.wireOp",EDGE,"E105.MirrorCS")}),-1.0]])]});
            var Q43;
            Q43=makeQuery(id+"F0.imprint","IMPRINT",FACE,{"disambiguationData":[TD([[makeQuery(id+"F0.imprint","IMPRINT",EDGE,{"derivedFrom":sQuery(id+"F0.wireOp",EDGE,"E96.MirrorCS")}),-1.0]])]});
            var Q44;
            Q44=makeQuery(id+"F0.imprint","IMPRINT",FACE,{"disambiguationData":[TD([[makeQuery(id+"F0.imprint","IMPRINT",EDGE,{"derivedFrom":sQuery(id+"F0.wireOp",EDGE,"E108.MirrorCS")}),-1.0]])]});
            var Q45;
            Q45=makeQuery(id+"F0.imprint","IMPRINT",FACE,{"disambiguationData":[TD([[makeQuery(id+"F0.imprint","IMPRINT",EDGE,{"derivedFrom":sQuery(id+"F0.wireOp",EDGE,"E97.MirrorCS")}),-1.0]])]});
            var Q46;
            Q46=makeQuery(id+"F0.imprint","IMPRINT",FACE,{"disambiguationData":[TD([[makeQuery(id+"F0.imprint","IMPRINT",EDGE,{"derivedFrom":sQuery(id+"F0.wireOp",EDGE,"E101.MirrorCS")}),-1.0]])]});
            var Q47;
            Q47=makeQuery(id+"F0.imprint","IMPRINT",FACE,{"disambiguationData":[TD([[makeQuery(id+"F0.imprint","IMPRINT",EDGE,{"derivedFrom":sQuery(id+"F0.wireOp",EDGE,"E110.MirrorCS")}),1.0]])]});
            var Q48;
            Q48=makeQuery(id+"F0.imprint","IMPRINT",FACE,{"disambiguationData":[TD([[makeQuery(id+"F0.imprint","IMPRINT",EDGE,{"derivedFrom":sQuery(id+"F0.wireOp",EDGE,"E93.MirrorCS")}),-1.0]])]});
            var Q49;
            Q49=makeQuery(id+"F0.imprint","IMPRINT",FACE,{"disambiguationData":[TD([[makeQuery(id+"F0.imprint","IMPRINT",EDGE,{"derivedFrom":sQuery(id+"F0.wireOp",EDGE,"E95.MirrorCS")}),1.0]])]});
            var Q50;
            Q50=makeQuery(id+"F0.imprint","IMPRINT",FACE,{"disambiguationData":[TD([[makeQuery(id+"F0.imprint","IMPRINT",EDGE,{"derivedFrom":sQuery(id+"F0.wireOp",EDGE,"E99.MirrorCS")}),1.0]])]});
            var Q51;
            Q51=makeQuery(id+"F0.imprint","IMPRINT",FACE,{"disambiguationData":[TD([[makeQuery(id+"F0.imprint","IMPRINT",EDGE,{"derivedFrom":sQuery(id+"F0.wireOp",EDGE,"E102.MirrorCS")}),1.0]])]});
            extrude(context, id + "F2", {"entities" : qUnion([Q0, Q1, Q2, Q3, Q4, Q5, Q6, Q7, Q8, Q9, Q10, Q11, Q12, Q13, Q14, Q15, Q16, Q17, Q18, Q19, Q20, Q21, Q22, Q23, Q24, Q25, Q26, Q27, Q28, Q29, Q30, Q31, Q32, Q33, Q34, Q35, Q36, Q37, Q38, Q39, Q40, Q41, Q42, Q43, Q44, Q45, Q46, Q47, Q48, Q49, Q50, Q51]), "depth" : 63.5 * mm});
        }
        {
            var Q0;
            Q0=makeQuery(id+"F2.opExtrude","SWEPT_FACE",FACE,{"disambiguationData":[OSD([sQuery(id+"F0.wireOp",EDGE,"E122.MirrorCS")])]});
            var sketch = newSketch(context, id + "F3", { "sketchPlane" : qUnion([Q0])});
            skArc(sketch, "E166", {"start": v(139.7, 63.5) * mm, "mid": v(69.85, 114.98) * mm, "end": v(0, 63.5) * mm});
            skLineSegment(sketch, "E167", {"start": v(152.4, 63.5) * mm, "end": v(152.4, 128.72) * mm});
            skLineSegment(sketch, "E168", {"start": v(-12.66, 63.5) * mm, "end": v(-12.66, 144.71) * mm, "construction": true});
            skLineSegment(sketch, "E169", {"start": v(152.4, 128.72) * mm, "end": v(-12.66, 128.72) * mm});
            skLineSegment(sketch, "E170", {"start": v(-12.66, 128.72) * mm, "end": v(-12.66, 63.5) * mm});
            skLineSegment(sketch, "E171", {"start": v(139.7, 63.5) * mm, "end": v(152.4, 63.5) * mm});
            skLineSegment(sketch, "E172", {"start": v(0, 63.5) * mm, "end": v(-12.66, 63.5) * mm});
            skSolve(sketch);
        }
        {
            var Q0;
            Q0=makeQuery(id+"F3.imprint","IMPRINT",FACE,{"disambiguationData":[TD([[makeQuery(id+"F3.imprint","IMPRINT",EDGE,{"derivedFrom":sQuery(id+"F3.wireOp",EDGE,"E166")}),-1.0]])]});
            var Q1;
            Q1=makeQuery(id+"F3.imprint","IMPRINT",FACE,{"disambiguationData":[TD([[makeQuery(id+"F3.imprint","IMPRINT",EDGE,{"derivedFrom":sQuery(id+"F3.wireOp",EDGE,"E171")}),-1.0]])]});
            var Q2;
            Q2=makeQuery(id+"F2.opExtrude","SWEPT_FACE",FACE,{"disambiguationData":[OSD([sQuery(id+"F0.wireOp",EDGE,"E0.left")])]});
            var Q3;
            Q3=makeQuery(id+"F1.opExtrude","SWEPT_FACE",FACE,{"disambiguationData":[OSD([sQuery(id+"F0.wireOp",EDGE,"E54.left")])]});
            var Q4;
            Q4=makeQuery(id+"F1.opExtrude","SWEPT_FACE",FACE,{"disambiguationData":[OSD([sQuery(id+"F0.wireOp",EDGE,"E132.MirrorCS")])]});
            extrude(context, id + "F4", {"entities" : qUnion([Q0, Q1, Q2, Q3, Q4]), "depth" : 4.83 * mm});
        }
    });
